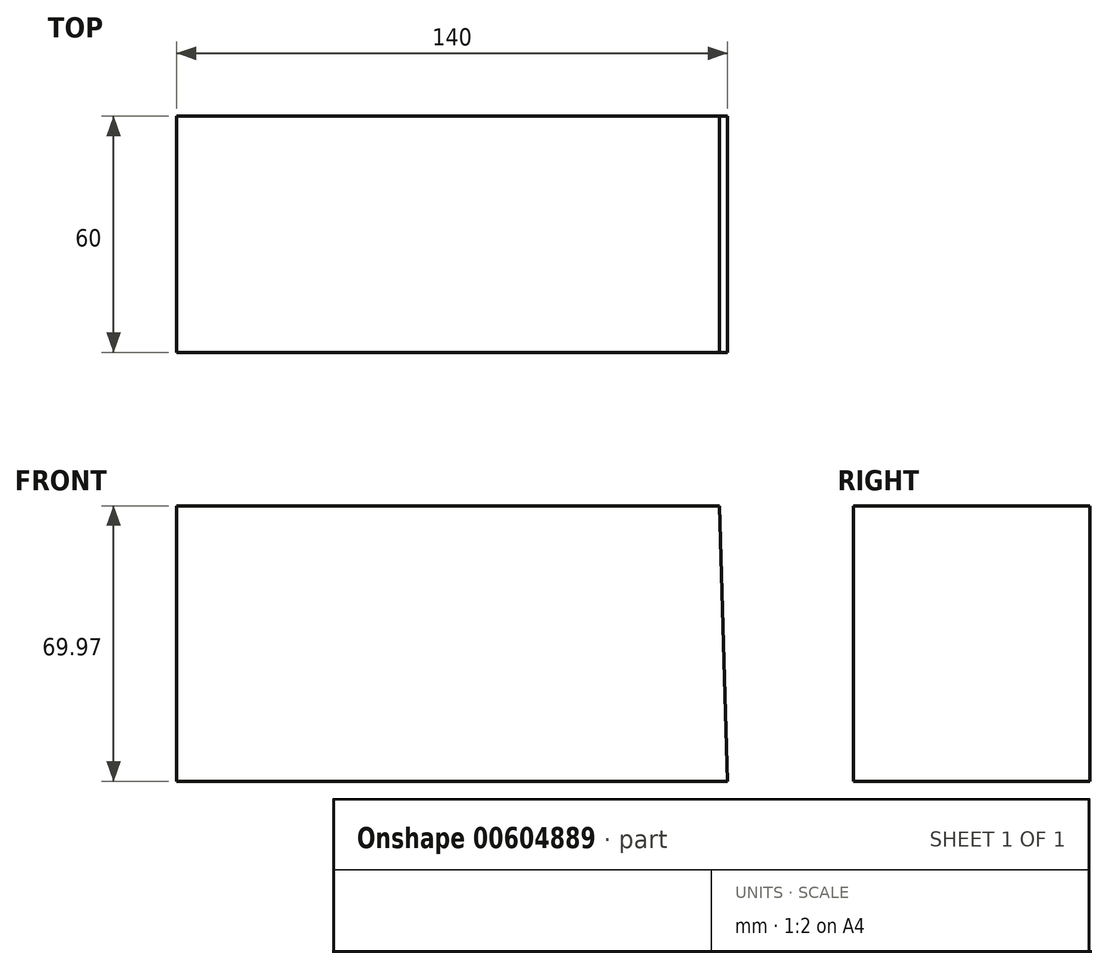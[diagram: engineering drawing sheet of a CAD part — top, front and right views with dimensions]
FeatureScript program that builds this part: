
annotation { "Feature Type Name" : "Feature", "Feature Type Description" : "" }
export const myFeature = defineFeature(function(context is Context, id is Id, definition is map)
    precondition{}
    {
        {
            var Q0;
            Q0=qCreatedBy(makeId("Front.planeOp"),FACE);
            var sketch = newSketch(context, id + "F0", { "sketchPlane" : qUnion([Q0])});
            skLineSegment(sketch, "E0", {"start": v(-69.45, 44.97) * mm, "end": v(-69.45, -25) * mm});
            skLineSegment(sketch, "E1", {"start": v(-69.45, 44.97) * mm, "end": v(68.48, 44.97) * mm});
            skLineSegment(sketch, "E2", {"start": v(-69.45, -25) * mm, "end": v(70.55, -25) * mm});
            skLineSegment(sketch, "E3", {"start": v(68.48, 44.97) * mm, "end": v(70.55, -25) * mm});
            skSolve(sketch);
        }
        {
            var Q0;
            Q0 = qSketchRegion(id + "F0", true);
            extrude(context, id + "F1", {"entities" : qUnion([Q0]), "depth" : 60 * mm, "offsetDistance" : 25.4 * mm});
        }
    });
